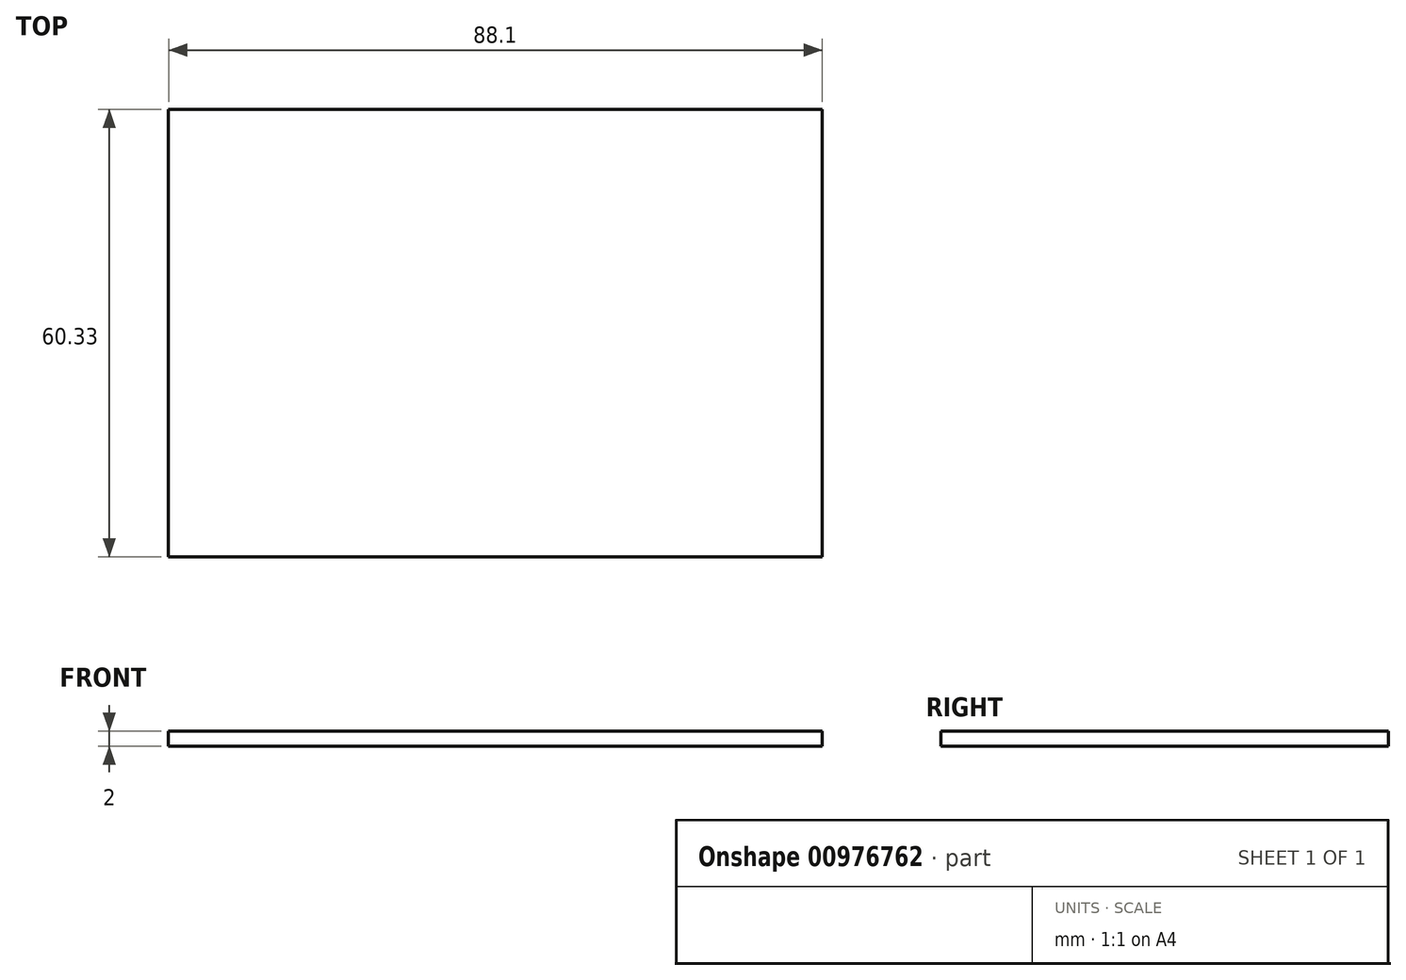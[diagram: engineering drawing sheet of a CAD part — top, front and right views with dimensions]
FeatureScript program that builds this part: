
annotation { "Feature Type Name" : "Feature", "Feature Type Description" : "" }
export const myFeature = defineFeature(function(context is Context, id is Id, definition is map)
    precondition{}
    {
        {
            var Q0;
            Q0=qCreatedBy(makeId("Top.planeOp"),FACE);
            var sketch = newSketch(context, id + "F0", { "sketchPlane" : qUnion([Q0])});
            skLineSegment(sketch, "E0.bottom", {"start": v(-41.78, 31.58) * mm, "end": v(46.32, 31.58) * mm});
            skLineSegment(sketch, "E0.top", {"start": v(-41.78, -28.75) * mm, "end": v(46.32, -28.75) * mm});
            skLineSegment(sketch, "E0.left", {"start": v(-41.78, 31.58) * mm, "end": v(-41.78, -28.75) * mm});
            skLineSegment(sketch, "E0.right", {"start": v(46.32, 31.58) * mm, "end": v(46.32, -28.75) * mm});
            skSolve(sketch);
        }
        {
            var Q0;
            Q0 = qSketchRegion(id + "F0", true);
            extrude(context, id + "F1", {"entities" : qUnion([Q0]), "depth" : 2 * mm, "offsetDistance" : 25 * mm});
        }
    });
